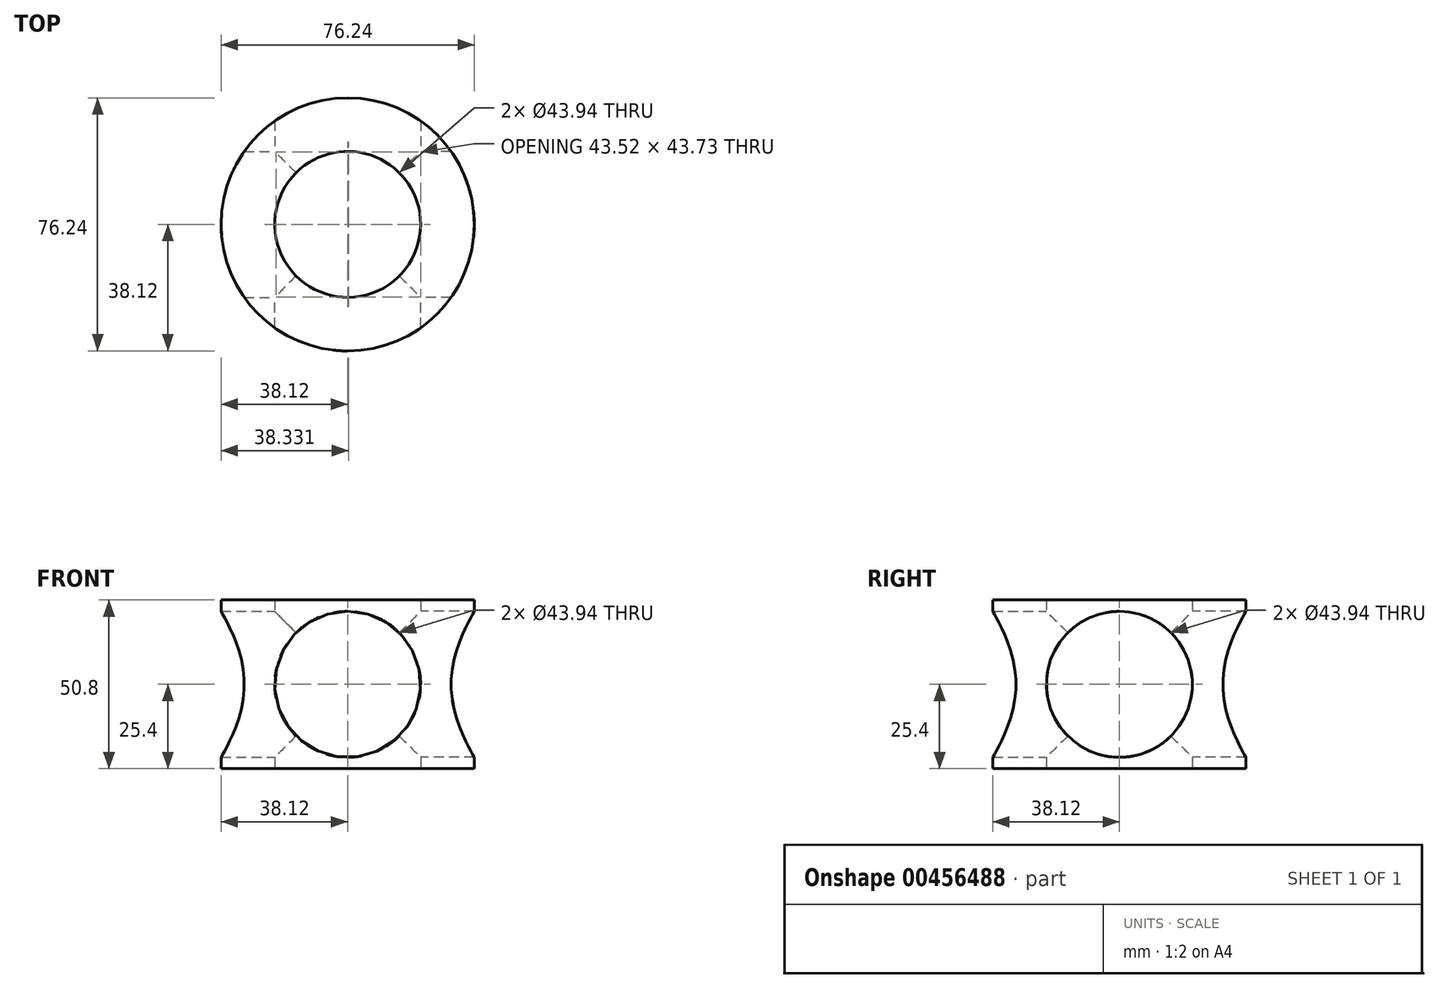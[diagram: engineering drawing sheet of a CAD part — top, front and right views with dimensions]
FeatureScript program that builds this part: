
annotation { "Feature Type Name" : "Feature", "Feature Type Description" : "" }
export const myFeature = defineFeature(function(context is Context, id is Id, definition is map)
    precondition{}
    {
        {
            var Q0;
            Q0=qCreatedBy(makeId("Top.planeOp"),FACE);
            var sketch = newSketch(context, id + "F0", { "sketchPlane" : qUnion([Q0])});
            skCircle(sketch, "E0", {"center": v(0, 0) * mm, "radius": 38.12 * mm});
            skSolve(sketch);
        }
        {
            var Q0;
            Q0=makeQuery(id+"F0.imprint","IMPRINT",FACE,{"disambiguationData":[TD([[makeQuery(id+"F0.imprint","IMPRINT",EDGE,{"derivedFrom":sQuery(id+"F0.wireOp",EDGE,"E0")}),1.0]])]});
            var Q1;
            Q1=sQuery(id+"F0.wireOp",EDGE,"E0");
            extrude(context, id + "F1", {"entities" : qUnion([Q0]), "surfaceEntities" : qUnion([Q1]), "depth" : 50.8 * mm, "offsetDistance" : 25.4 * mm});
        }
        {
            var Q0;
            Q0=qCreatedBy(makeId("Top.planeOp"),FACE);
            var sketch = newSketch(context, id + "F2", { "sketchPlane" : qUnion([Q0])});
            skCircle(sketch, "E1", {"center": v(0, 0) * mm, "radius": 21.97 * mm});
            skSolve(sketch);
        }
        {
            var Q0;
            Q0=makeQuery(id+"F2.imprint","IMPRINT",FACE,{"disambiguationData":[TD([[makeQuery(id+"F2.imprint","IMPRINT",EDGE,{"derivedFrom":sQuery(id+"F2.wireOp",EDGE,"E1")}),1.0]])]});
            var Q1;
            Q1=sQuery(id+"F2.wireOp",EDGE,"E1");
            extrude(context, id + "F3", {"entities" : qUnion([Q0]), "operationType" : NewBodyOperationType.REMOVE, "surfaceEntities" : qUnion([Q1]), "depth" : 63.5 * mm, "offsetDistance" : 25.4 * mm});
        }
        {
            var Q0;
            Q0=qCreatedBy(makeId("Front.planeOp"),FACE);
            var sketch = newSketch(context, id + "F4", { "sketchPlane" : qUnion([Q0])});
            skCircle(sketch, "E2", {"center": v(0, 25.4) * mm, "radius": 21.97 * mm});
            skLineSegment(sketch, "E3", {"start": v(0, 50.8) * mm, "end": v(0, 0) * mm});
            skSolve(sketch);
        }
        {
            var Q0;
            Q0 = qSketchRegion(id + "F4", true);
            extrude(context, id + "F5", {"entities" : qUnion([Q0]), "operationType" : NewBodyOperationType.REMOVE, "oppositeDirection" : true, "depth" : 76.2 * mm, "offsetDistance" : 25.4 * mm});
        }
        {
            var Q0;
            Q0=qCreatedBy(makeId("Front.planeOp"),FACE);
            var sketch = newSketch(context, id + "F6", { "sketchPlane" : qUnion([Q0])});
            skCircle(sketch, "E4", {"center": v(0, 25.4) * mm, "radius": 21.97 * mm});
            skLineSegment(sketch, "E5", {"start": v(0, 50.8) * mm, "end": v(0, 0) * mm});
            skSolve(sketch);
        }
        {
            var Q0;
            Q0 = qSketchRegion(id + "F6", true);
            extrude(context, id + "F7", {"entities" : qUnion([Q0]), "operationType" : NewBodyOperationType.REMOVE, "depth" : 76.2 * mm, "offsetDistance" : 25.4 * mm});
        }
        {
            var Q0;
            Q0=qCreatedBy(makeId("Right.planeOp"),FACE);
            var sketch = newSketch(context, id + "F8", { "sketchPlane" : qUnion([Q0])});
            skCircle(sketch, "E6", {"center": v(0, 25.4) * mm, "radius": 21.97 * mm});
            skLineSegment(sketch, "E7", {"start": v(0, 50.8) * mm, "end": v(0, 0) * mm});
            skSolve(sketch);
        }
        {
            var Q0;
            Q0=makeQuery(id+"F8.imprint","IMPRINT",FACE,{"disambiguationData":[TD([[makeQuery(id+"F8.imprint","IMPRINT",EDGE,{"derivedFrom":sQuery(id+"F8.wireOp",EDGE,"E6")}),1.0]])]});
            var Q1;
            Q1=sQuery(id+"F8.wireOp",EDGE,"E6");
            extrude(context, id + "F9", {"entities" : qUnion([Q0]), "operationType" : NewBodyOperationType.REMOVE, "surfaceEntities" : qUnion([Q1]), "oppositeDirection" : true, "depth" : 76.2 * mm, "offsetDistance" : 25.4 * mm});
        }
        {
            var Q0;
            Q0=qCreatedBy(makeId("Right.planeOp"),FACE);
            var sketch = newSketch(context, id + "F10", { "sketchPlane" : qUnion([Q0])});
            skCircle(sketch, "E8", {"center": v(0, 25.4) * mm, "radius": 21.97 * mm});
            skLineSegment(sketch, "E9", {"start": v(0, 50.8) * mm, "end": v(0, 0) * mm, "construction": true});
            skSolve(sketch);
        }
        {
            var Q0;
            Q0 = qSketchRegion(id + "F10", true);
            extrude(context, id + "F11", {"entities" : qUnion([Q0]), "operationType" : NewBodyOperationType.REMOVE, "depth" : 76.2 * mm, "offsetDistance" : 25.4 * mm});
        }
    });
